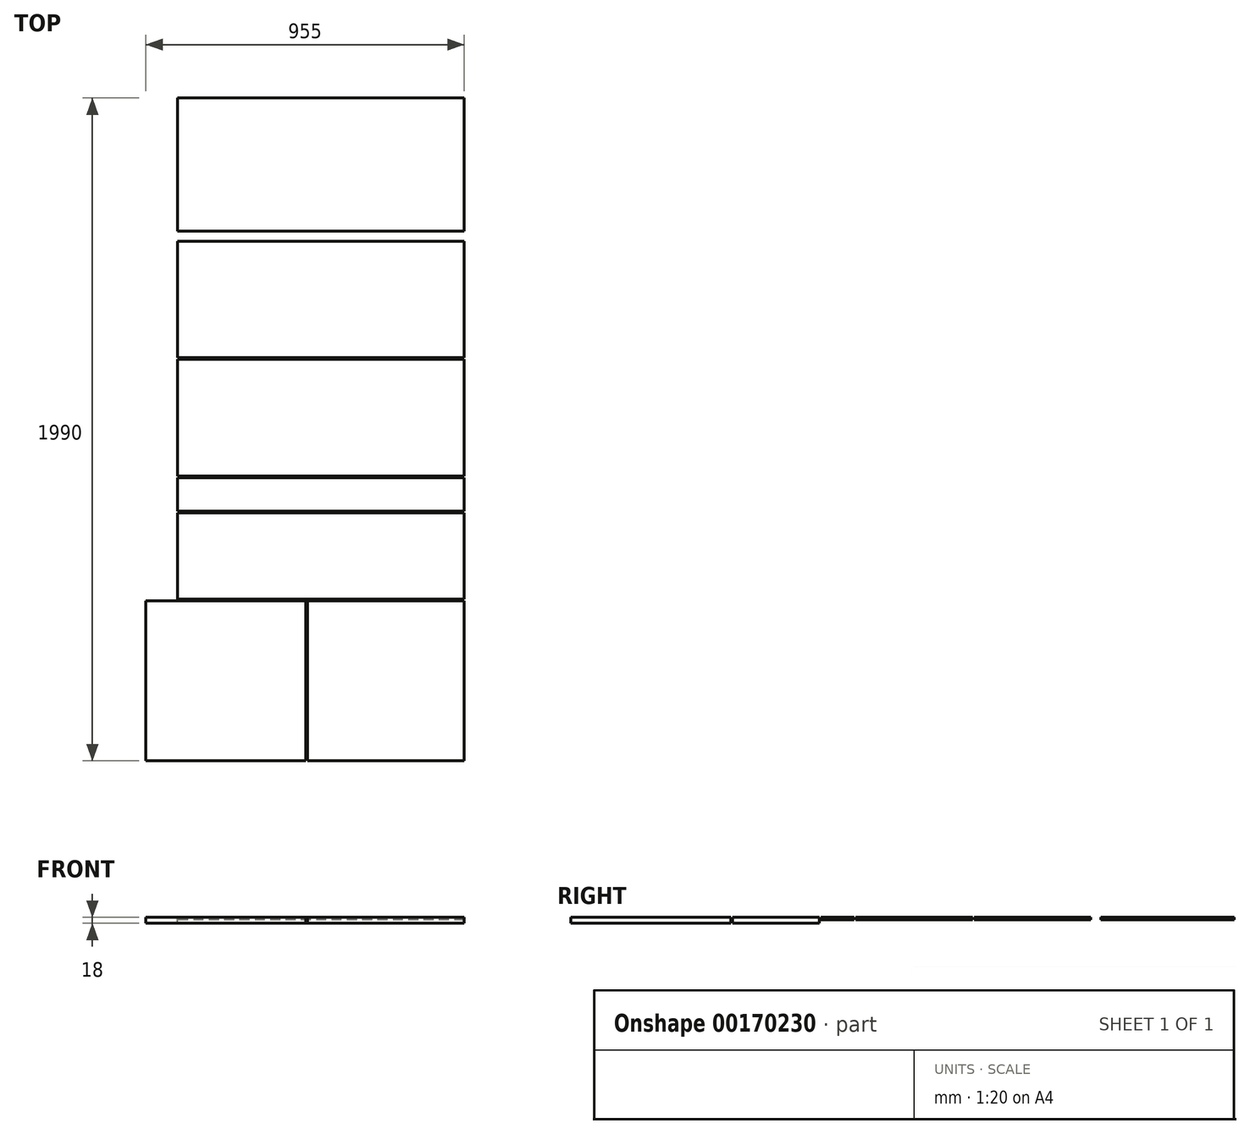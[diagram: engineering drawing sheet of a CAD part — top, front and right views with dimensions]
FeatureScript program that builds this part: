
annotation { "Feature Type Name" : "Feature", "Feature Type Description" : "" }
export const myFeature = defineFeature(function(context is Context, id is Id, definition is map)
    precondition{}
    {
        {
            var Q0;
            Q0=qCreatedBy(makeId("Top.planeOp"),FACE);
            var sketch = newSketch(context, id + "F0", { "sketchPlane" : qUnion([Q0])});
            skLineSegment(sketch, "E0.bottom", {"start": v(-241.6, -111.48) * mm, "end": v(238.4, -111.48) * mm});
            skLineSegment(sketch, "E0.top", {"start": v(-241.6, 368.52) * mm, "end": v(238.4, 368.52) * mm});
            skLineSegment(sketch, "E0.left", {"start": v(-241.6, -111.48) * mm, "end": v(-241.6, 368.52) * mm});
            skLineSegment(sketch, "E0.right", {"start": v(238.4, -111.48) * mm, "end": v(238.4, 368.52) * mm});
            skLineSegment(sketch, "E1.bottom", {"start": v(243.4, -111.48) * mm, "end": v(713.4, -111.48) * mm});
            skLineSegment(sketch, "E1.top", {"start": v(243.4, 368.52) * mm, "end": v(713.4, 368.52) * mm});
            skLineSegment(sketch, "E1.left", {"start": v(243.4, -111.48) * mm, "end": v(243.4, 368.52) * mm});
            skLineSegment(sketch, "E1.right", {"start": v(713.4, -111.48) * mm, "end": v(713.4, 368.52) * mm});
            skLineSegment(sketch, "E2", {"start": v(238.4, -111.48) * mm, "end": v(243.4, -111.48) * mm, "construction": true});
            skLineSegment(sketch, "E3.bottom", {"start": v(713.4, 373.52) * mm, "end": v(-146.6, 373.52) * mm});
            skLineSegment(sketch, "E3.top", {"start": v(713.4, 633.52) * mm, "end": v(-146.6, 633.52) * mm});
            skLineSegment(sketch, "E3.left", {"start": v(713.4, 373.52) * mm, "end": v(713.4, 633.52) * mm});
            skLineSegment(sketch, "E3.right", {"start": v(-146.6, 373.52) * mm, "end": v(-146.6, 633.52) * mm});
            skLineSegment(sketch, "E4", {"start": v(713.4, 368.52) * mm, "end": v(713.4, 373.52) * mm, "construction": true});
            skLineSegment(sketch, "E5.bottom", {"start": v(713.4, 638.52) * mm, "end": v(-146.6, 638.52) * mm});
            skLineSegment(sketch, "E5.top", {"start": v(713.4, 738.52) * mm, "end": v(-146.6, 738.52) * mm});
            skLineSegment(sketch, "E5.left", {"start": v(713.4, 638.52) * mm, "end": v(713.4, 738.52) * mm});
            skLineSegment(sketch, "E5.right", {"start": v(-146.6, 638.52) * mm, "end": v(-146.6, 738.52) * mm});
            skLineSegment(sketch, "E6.bottom", {"start": v(713.4, 743.52) * mm, "end": v(-146.6, 743.52) * mm});
            skLineSegment(sketch, "E6.top", {"start": v(713.4, 1093.52) * mm, "end": v(-146.6, 1093.52) * mm});
            skLineSegment(sketch, "E6.left", {"start": v(713.4, 743.52) * mm, "end": v(713.4, 1093.52) * mm});
            skLineSegment(sketch, "E6.right", {"start": v(-146.6, 743.52) * mm, "end": v(-146.6, 1093.52) * mm});
            skLineSegment(sketch, "E7.bottom", {"start": v(713.4, 1098.52) * mm, "end": v(-146.6, 1098.52) * mm});
            skLineSegment(sketch, "E7.top", {"start": v(713.4, 1448.52) * mm, "end": v(-146.6, 1448.52) * mm});
            skLineSegment(sketch, "E7.left", {"start": v(713.4, 1098.52) * mm, "end": v(713.4, 1448.52) * mm});
            skLineSegment(sketch, "E7.right", {"start": v(-146.6, 1098.52) * mm, "end": v(-146.6, 1448.52) * mm});
            skLineSegment(sketch, "E8.bottom", {"start": v(713.4, 1478.52) * mm, "end": v(-146.6, 1478.52) * mm});
            skLineSegment(sketch, "E8.top", {"start": v(713.4, 1878.52) * mm, "end": v(-146.6, 1878.52) * mm});
            skLineSegment(sketch, "E8.left", {"start": v(713.4, 1478.52) * mm, "end": v(713.4, 1878.52) * mm});
            skLineSegment(sketch, "E8.right", {"start": v(-146.6, 1478.52) * mm, "end": v(-146.6, 1878.52) * mm});
            skLineSegment(sketch, "E9", {"start": v(713.4, 633.52) * mm, "end": v(713.4, 638.52) * mm, "construction": true});
            skLineSegment(sketch, "E10", {"start": v(713.4, 738.52) * mm, "end": v(713.4, 743.52) * mm, "construction": true});
            skLineSegment(sketch, "E11", {"start": v(713.4, 1093.52) * mm, "end": v(713.4, 1098.52) * mm, "construction": true});
            skLineSegment(sketch, "E12", {"start": v(713.4, 1448.52) * mm, "end": v(713.4, 1478.52) * mm, "construction": true});
            skSolve(sketch);
        }
        {
            var Q0;
            Q0=makeQuery(id+"F0.imprint","IMPRINT",FACE,{"disambiguationData":[TD([[makeQuery(id+"F0.imprint","IMPRINT",EDGE,{"derivedFrom":sQuery(id+"F0.wireOp",EDGE,"E0.bottom")}),1.0]])]});
            var Q1;
            Q1=makeQuery(id+"F0.imprint","IMPRINT",FACE,{"disambiguationData":[TD([[makeQuery(id+"F0.imprint","IMPRINT",EDGE,{"derivedFrom":sQuery(id+"F0.wireOp",EDGE,"E1.bottom")}),1.0]])]});
            var Q2;
            Q2=makeQuery(id+"F0.imprint","IMPRINT",FACE,{"disambiguationData":[TD([[makeQuery(id+"F0.imprint","IMPRINT",EDGE,{"derivedFrom":sQuery(id+"F0.wireOp",EDGE,"E3.bottom")}),-1.0]])]});
            extrude(context, id + "F1", {"entities" : qUnion([Q0, Q1, Q2]), "oppositeDirection" : true, "depth" : 18 * mm});
        }
        {
            var Q0;
            Q0=makeQuery(id+"F0.imprint","IMPRINT",FACE,{"disambiguationData":[TD([[makeQuery(id+"F0.imprint","IMPRINT",EDGE,{"derivedFrom":sQuery(id+"F0.wireOp",EDGE,"E5.bottom")}),-1.0]])]});
            var Q1;
            Q1=makeQuery(id+"F0.imprint","IMPRINT",FACE,{"disambiguationData":[TD([[makeQuery(id+"F0.imprint","IMPRINT",EDGE,{"derivedFrom":sQuery(id+"F0.wireOp",EDGE,"E6.bottom")}),-1.0]])]});
            var Q2;
            Q2=makeQuery(id+"F0.imprint","IMPRINT",FACE,{"disambiguationData":[TD([[makeQuery(id+"F0.imprint","IMPRINT",EDGE,{"derivedFrom":sQuery(id+"F0.wireOp",EDGE,"E7.bottom")}),-1.0]])]});
            var Q3;
            Q3=makeQuery(id+"F0.imprint","IMPRINT",FACE,{"disambiguationData":[TD([[makeQuery(id+"F0.imprint","IMPRINT",EDGE,{"derivedFrom":sQuery(id+"F0.wireOp",EDGE,"E8.bottom")}),-1.0]])]});
            extrude(context, id + "F2", {"entities" : qUnion([Q0, Q1, Q2, Q3]), "oppositeDirection" : true, "depth" : 7 * mm});
        }
    });
